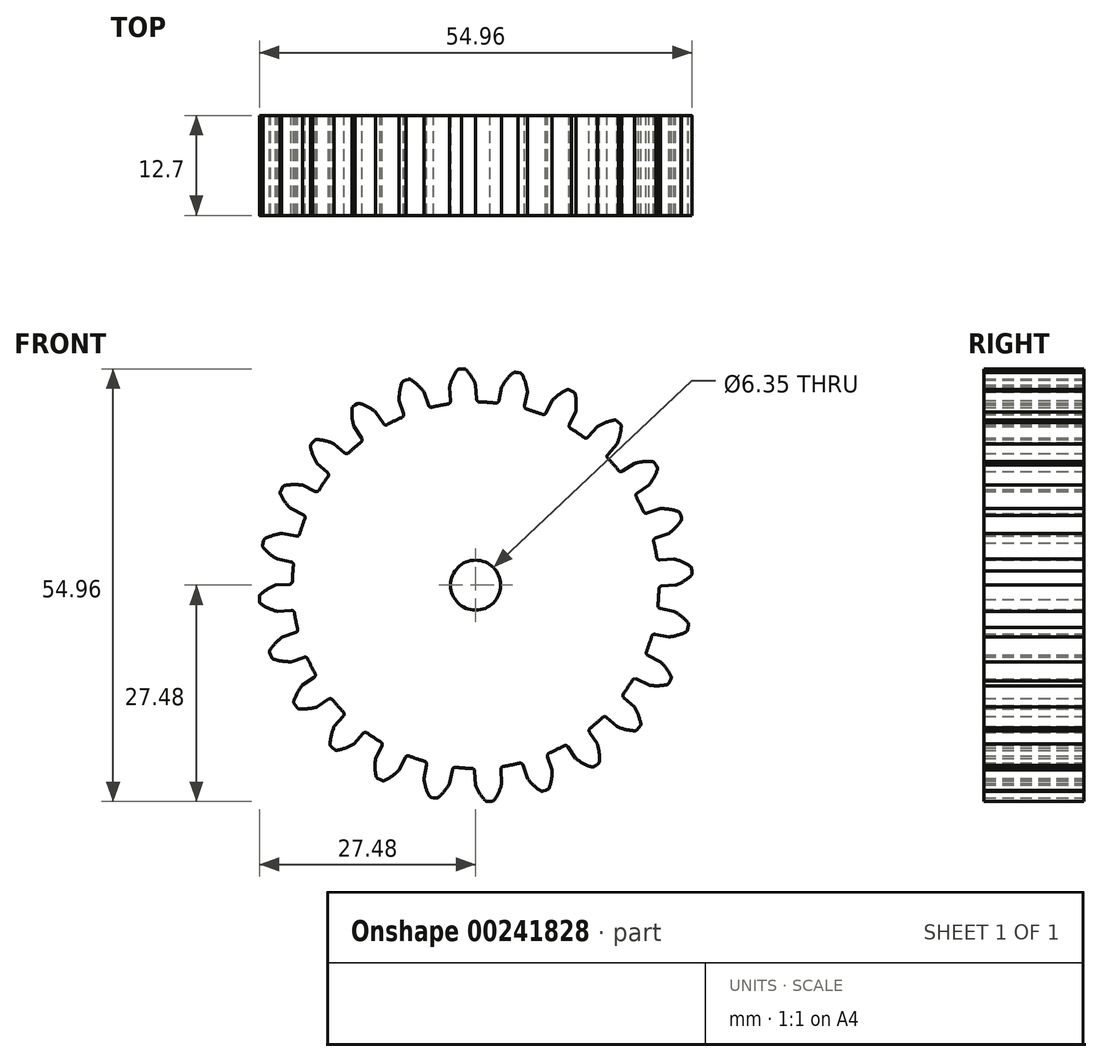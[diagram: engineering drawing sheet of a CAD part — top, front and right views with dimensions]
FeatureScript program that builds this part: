
annotation { "Feature Type Name" : "Feature", "Feature Type Description" : "" }
export const myFeature = defineFeature(function(context is Context, id is Id, definition is map)
    precondition{}
    {
        {
            var Q0;
            Q0=qCreatedBy(makeId("Front.planeOp"),FACE);
            var sketch = newSketch(context, id + "F0", { "sketchPlane" : qUnion([Q0])});
            skArc(sketch, "E0", {"start": v(-3.52, 23.02) * mm, "mid": v(-4.54, 22.84) * mm, "end": v(-5.55, 22.61) * mm});
            skArc(sketch, "E1.trimOffspring", {"start": v(0, 25.4) * mm, "mid": v(-0.5, 26.43) * mm, "end": v(-1.2, 27.35) * mm});
            skLineSegment(sketch, "E2", {"start": v(0, 25.4) * mm, "end": v(0.12, 23.63) * mm});
            skLineSegment(sketch, "E3", {"start": v(-1.5, 27.48) * mm, "end": v(-1.8, 27.46) * mm});
            skLineSegment(sketch, "E4.MirrorCS", {"start": v(-2.1, 27.44) * mm, "end": v(-1.8, 27.46) * mm});
            skArc(sketch, "E5.MirrorCS", {"start": v(-3.32, 25.18) * mm, "mid": v(-2.95, 26.27) * mm, "end": v(-2.39, 27.27) * mm});
            skLineSegment(sketch, "E6.MirrorCS", {"start": v(-3.32, 25.18) * mm, "end": v(-3.2, 23.42) * mm});
            skPoint(sketch, "E7.visualSharp", {"position": v(-2.28, 27.42) * mm});
            skArc(sketch, "E7.filletArc", {"start": v(-2.1, 27.44) * mm, "mid": v(-2.27, 27.39) * mm, "end": v(-2.39, 27.27) * mm});
            skPoint(sketch, "E8.visualSharp", {"position": v(-1.31, 27.49) * mm});
            skArc(sketch, "E8.filletArc", {"start": v(-1.2, 27.35) * mm, "mid": v(-1.33, 27.45) * mm, "end": v(-1.5, 27.48) * mm});
            skPoint(sketch, "E9.visualSharp", {"position": v(0.14, 23.28) * mm});
            skArc(sketch, "E9.filletArc", {"start": v(0.12, 23.63) * mm, "mid": v(0.23, 23.38) * mm, "end": v(0.49, 23.28) * mm});
            skPoint(sketch, "E10.visualSharp", {"position": v(-3.18, 23.07) * mm});
            skArc(sketch, "E10.filletArc", {"start": v(-3.52, 23.02) * mm, "mid": v(-3.28, 23.15) * mm, "end": v(-3.2, 23.42) * mm});
            skPoint(sketch, "E11.1.0", {"position": v(-8.38, 26.2) * mm});
            skPoint(sketch, "E11.1.1", {"position": v(-9.04, 21.46) * mm});
            skArc(sketch, "E11.1.2", {"start": v(-6.57, 24.53) * mm, "mid": v(-7.33, 25.4) * mm, "end": v(-8.23, 26.1) * mm});
            skArc(sketch, "E11.1.3", {"start": v(-9.72, 23.47) * mm, "mid": v(-9.65, 24.61) * mm, "end": v(-9.37, 25.72) * mm});
            skLineSegment(sketch, "E11.1.4", {"start": v(-9.72, 23.47) * mm, "end": v(-9.15, 21.8) * mm});
            skPoint(sketch, "E11.1.5", {"position": v(-9.3, 25.9) * mm});
            skLineSegment(sketch, "E11.1.6", {"start": v(-6.57, 24.53) * mm, "end": v(-6, 22.86) * mm});
            skLineSegment(sketch, "E11.1.7", {"start": v(-9.14, 25.96) * mm, "end": v(-8.85, 26.06) * mm});
            skArc(sketch, "E11.1.8", {"start": v(-9.14, 25.96) * mm, "mid": v(-9.28, 25.87) * mm, "end": v(-9.37, 25.72) * mm});
            skArc(sketch, "E11.1.9", {"start": v(-8.23, 26.1) * mm, "mid": v(-8.39, 26.17) * mm, "end": v(-8.55, 26.15) * mm});
            skLineSegment(sketch, "E11.1.10", {"start": v(-8.55, 26.15) * mm, "end": v(-8.85, 26.06) * mm});
            skArc(sketch, "E11.1.11", {"start": v(-6, 22.86) * mm, "mid": v(-5.83, 22.65) * mm, "end": v(-5.55, 22.61) * mm});
            skArc(sketch, "E11.1.12", {"start": v(-9.36, 21.32) * mm, "mid": v(-9.16, 21.51) * mm, "end": v(-9.15, 21.8) * mm});
            skPoint(sketch, "E11.2.0", {"position": v(-14.88, 23.15) * mm});
            skPoint(sketch, "E11.2.1", {"position": v(-14.28, 18.39) * mm});
            skArc(sketch, "E11.2.2", {"start": v(-12.7, 22) * mm, "mid": v(-13.65, 22.63) * mm, "end": v(-14.7, 23.1) * mm});
            skArc(sketch, "E11.2.3", {"start": v(-15.46, 20.15) * mm, "mid": v(-15.69, 21.28) * mm, "end": v(-15.7, 22.42) * mm});
            skLineSegment(sketch, "E11.2.4", {"start": v(-15.46, 20.15) * mm, "end": v(-14.48, 18.68) * mm});
            skPoint(sketch, "E11.2.5", {"position": v(-15.69, 22.6) * mm});
            skLineSegment(sketch, "E11.2.6", {"start": v(-12.7, 22) * mm, "end": v(-11.72, 20.53) * mm});
            skLineSegment(sketch, "E11.2.7", {"start": v(-15.54, 22.7) * mm, "end": v(-15.29, 22.88) * mm});
            skArc(sketch, "E11.2.8", {"start": v(-15.54, 22.7) * mm, "mid": v(-15.66, 22.58) * mm, "end": v(-15.7, 22.42) * mm});
            skArc(sketch, "E11.2.9", {"start": v(-14.7, 23.1) * mm, "mid": v(-14.87, 23.1) * mm, "end": v(-15.03, 23.05) * mm});
            skLineSegment(sketch, "E11.2.10", {"start": v(-15.03, 23.05) * mm, "end": v(-15.29, 22.88) * mm});
            skArc(sketch, "E11.2.11", {"start": v(-11.72, 20.53) * mm, "mid": v(-11.5, 20.37) * mm, "end": v(-11.22, 20.4) * mm});
            skArc(sketch, "E11.2.12", {"start": v(-14.56, 18.17) * mm, "mid": v(-14.42, 18.41) * mm, "end": v(-14.48, 18.68) * mm});
            skPoint(sketch, "E11.3.0", {"position": v(-20.36, 18.5) * mm});
            skPoint(sketch, "E11.3.1", {"position": v(-18.56, 14.06) * mm});
            skArc(sketch, "E11.3.2", {"start": v(-17.96, 17.96) * mm, "mid": v(-19.05, 18.33) * mm, "end": v(-20.18, 18.5) * mm});
            skArc(sketch, "E11.3.3", {"start": v(-20.15, 15.46) * mm, "mid": v(-20.66, 16.5) * mm, "end": v(-20.97, 17.6) * mm});
            skLineSegment(sketch, "E11.3.4", {"start": v(-20.15, 15.46) * mm, "end": v(-18.82, 14.3) * mm});
            skPoint(sketch, "E11.3.5", {"position": v(-21, 17.77) * mm});
            skLineSegment(sketch, "E11.3.6", {"start": v(-17.96, 17.96) * mm, "end": v(-16.63, 16.8) * mm});
            skLineSegment(sketch, "E11.3.7", {"start": v(-20.9, 17.91) * mm, "end": v(-20.7, 18.15) * mm});
            skArc(sketch, "E11.3.8", {"start": v(-20.9, 17.91) * mm, "mid": v(-20.97, 17.76) * mm, "end": v(-20.97, 17.6) * mm});
            skArc(sketch, "E11.3.9", {"start": v(-20.18, 18.5) * mm, "mid": v(-20.35, 18.47) * mm, "end": v(-20.48, 18.37) * mm});
            skLineSegment(sketch, "E11.3.10", {"start": v(-20.48, 18.37) * mm, "end": v(-20.7, 18.15) * mm});
            skArc(sketch, "E11.3.11", {"start": v(-16.63, 16.8) * mm, "mid": v(-16.37, 16.7) * mm, "end": v(-16.12, 16.8) * mm});
            skArc(sketch, "E11.3.12", {"start": v(-18.76, 13.78) * mm, "mid": v(-18.7, 14.05) * mm, "end": v(-18.82, 14.3) * mm});
            skPoint(sketch, "E11.4.0", {"position": v(-24.46, 12.6) * mm});
            skPoint(sketch, "E11.4.1", {"position": v(-21.56, 8.78) * mm});
            skArc(sketch, "E11.4.2", {"start": v(-22, 12.7) * mm, "mid": v(-23.14, 12.78) * mm, "end": v(-24.28, 12.64) * mm});
            skArc(sketch, "E11.4.3", {"start": v(-23.47, 9.72) * mm, "mid": v(-24.22, 10.58) * mm, "end": v(-24.81, 11.57) * mm});
            skLineSegment(sketch, "E11.4.4", {"start": v(-23.47, 9.72) * mm, "end": v(-21.88, 8.94) * mm});
            skPoint(sketch, "E11.4.5", {"position": v(-24.89, 11.73) * mm});
            skLineSegment(sketch, "E11.4.6", {"start": v(-22, 12.7) * mm, "end": v(-20.4, 11.92) * mm});
            skLineSegment(sketch, "E11.4.7", {"start": v(-24.81, 11.9) * mm, "end": v(-24.68, 12.17) * mm});
            skArc(sketch, "E11.4.8", {"start": v(-24.81, 11.9) * mm, "mid": v(-24.85, 11.73) * mm, "end": v(-24.81, 11.57) * mm});
            skArc(sketch, "E11.4.9", {"start": v(-24.28, 12.64) * mm, "mid": v(-24.43, 12.57) * mm, "end": v(-24.54, 12.45) * mm});
            skLineSegment(sketch, "E11.4.10", {"start": v(-24.54, 12.45) * mm, "end": v(-24.68, 12.17) * mm});
            skArc(sketch, "E11.4.11", {"start": v(-20.4, 11.92) * mm, "mid": v(-20.13, 11.9) * mm, "end": v(-19.92, 12.06) * mm});
            skArc(sketch, "E11.4.12", {"start": v(-21.7, 8.46) * mm, "mid": v(-21.7, 8.73) * mm, "end": v(-21.88, 8.94) * mm});
            skPoint(sketch, "E11.5.0", {"position": v(-26.89, 5.84) * mm});
            skPoint(sketch, "E11.5.1", {"position": v(-23.1, 2.9) * mm});
            skArc(sketch, "E11.5.2", {"start": v(-24.53, 6.57) * mm, "mid": v(-25.66, 6.35) * mm, "end": v(-26.73, 5.93) * mm});
            skArc(sketch, "E11.5.3", {"start": v(-25.18, 3.32) * mm, "mid": v(-26.14, 3.95) * mm, "end": v(-26.96, 4.75) * mm});
            skLineSegment(sketch, "E11.5.4", {"start": v(-25.18, 3.32) * mm, "end": v(-23.45, 2.97) * mm});
            skPoint(sketch, "E11.5.5", {"position": v(-27.08, 4.9) * mm});
            skLineSegment(sketch, "E11.5.6", {"start": v(-24.53, 6.57) * mm, "end": v(-22.8, 6.23) * mm});
            skLineSegment(sketch, "E11.5.7", {"start": v(-27.05, 5.07) * mm, "end": v(-27, 5.37) * mm});
            skArc(sketch, "E11.5.8", {"start": v(-27.05, 5.07) * mm, "mid": v(-27.04, 4.9) * mm, "end": v(-26.96, 4.75) * mm});
            skArc(sketch, "E11.5.9", {"start": v(-26.73, 5.93) * mm, "mid": v(-26.86, 5.82) * mm, "end": v(-26.93, 5.67) * mm});
            skLineSegment(sketch, "E11.5.10", {"start": v(-26.93, 5.67) * mm, "end": v(-27, 5.37) * mm});
            skArc(sketch, "E11.5.11", {"start": v(-22.8, 6.23) * mm, "mid": v(-22.53, 6.28) * mm, "end": v(-22.36, 6.5) * mm});
            skArc(sketch, "E11.5.12", {"start": v(-23.14, 2.55) * mm, "mid": v(-23.21, 2.82) * mm, "end": v(-23.45, 2.97) * mm});
            skPoint(sketch, "E11.6.0", {"position": v(-27.49, -1.31) * mm});
            skPoint(sketch, "E11.6.1", {"position": v(-23.07, -3.18) * mm});
            skArc(sketch, "E11.6.2", {"start": v(-25.4, 0) * mm, "mid": v(-26.43, -0.5) * mm, "end": v(-27.35, -1.2) * mm});
            skArc(sketch, "E11.6.3", {"start": v(-25.18, -3.32) * mm, "mid": v(-26.27, -2.95) * mm, "end": v(-27.27, -2.39) * mm});
            skLineSegment(sketch, "E11.6.4", {"start": v(-25.18, -3.32) * mm, "end": v(-23.42, -3.2) * mm});
            skPoint(sketch, "E11.6.5", {"position": v(-27.42, -2.28) * mm});
            skLineSegment(sketch, "E11.6.6", {"start": v(-25.4, 0) * mm, "end": v(-23.63, 0.12) * mm});
            skLineSegment(sketch, "E11.6.7", {"start": v(-27.44, -2.1) * mm, "end": v(-27.46, -1.8) * mm});
            skArc(sketch, "E11.6.8", {"start": v(-27.44, -2.1) * mm, "mid": v(-27.39, -2.27) * mm, "end": v(-27.27, -2.39) * mm});
            skArc(sketch, "E11.6.9", {"start": v(-27.35, -1.2) * mm, "mid": v(-27.45, -1.33) * mm, "end": v(-27.48, -1.5) * mm});
            skLineSegment(sketch, "E11.6.10", {"start": v(-27.48, -1.5) * mm, "end": v(-27.46, -1.8) * mm});
            skArc(sketch, "E11.6.11", {"start": v(-23.63, 0.12) * mm, "mid": v(-23.38, 0.23) * mm, "end": v(-23.28, 0.49) * mm});
            skArc(sketch, "E11.6.12", {"start": v(-23.02, -3.52) * mm, "mid": v(-23.15, -3.28) * mm, "end": v(-23.42, -3.2) * mm});
            skPoint(sketch, "E11.7.0", {"position": v(-26.2, -8.38) * mm});
            skPoint(sketch, "E11.7.1", {"position": v(-21.46, -9.04) * mm});
            skArc(sketch, "E11.7.2", {"start": v(-24.53, -6.57) * mm, "mid": v(-25.4, -7.33) * mm, "end": v(-26.1, -8.23) * mm});
            skArc(sketch, "E11.7.3", {"start": v(-23.47, -9.72) * mm, "mid": v(-24.61, -9.65) * mm, "end": v(-25.72, -9.37) * mm});
            skLineSegment(sketch, "E11.7.4", {"start": v(-23.47, -9.72) * mm, "end": v(-21.8, -9.15) * mm});
            skPoint(sketch, "E11.7.5", {"position": v(-25.9, -9.3) * mm});
            skLineSegment(sketch, "E11.7.6", {"start": v(-24.53, -6.57) * mm, "end": v(-22.86, -6) * mm});
            skLineSegment(sketch, "E11.7.7", {"start": v(-25.96, -9.14) * mm, "end": v(-26.06, -8.85) * mm});
            skArc(sketch, "E11.7.8", {"start": v(-25.96, -9.14) * mm, "mid": v(-25.87, -9.28) * mm, "end": v(-25.72, -9.37) * mm});
            skArc(sketch, "E11.7.9", {"start": v(-26.1, -8.23) * mm, "mid": v(-26.17, -8.39) * mm, "end": v(-26.15, -8.55) * mm});
            skLineSegment(sketch, "E11.7.10", {"start": v(-26.15, -8.55) * mm, "end": v(-26.06, -8.85) * mm});
            skArc(sketch, "E11.7.11", {"start": v(-22.86, -6) * mm, "mid": v(-22.65, -5.83) * mm, "end": v(-22.61, -5.55) * mm});
            skArc(sketch, "E11.7.12", {"start": v(-21.32, -9.36) * mm, "mid": v(-21.51, -9.16) * mm, "end": v(-21.8, -9.15) * mm});
            skPoint(sketch, "E11.8.0", {"position": v(-23.15, -14.88) * mm});
            skPoint(sketch, "E11.8.1", {"position": v(-18.39, -14.28) * mm});
            skArc(sketch, "E11.8.2", {"start": v(-22, -12.7) * mm, "mid": v(-22.63, -13.65) * mm, "end": v(-23.1, -14.7) * mm});
            skArc(sketch, "E11.8.3", {"start": v(-20.15, -15.46) * mm, "mid": v(-21.28, -15.69) * mm, "end": v(-22.42, -15.7) * mm});
            skLineSegment(sketch, "E11.8.4", {"start": v(-20.15, -15.46) * mm, "end": v(-18.68, -14.48) * mm});
            skPoint(sketch, "E11.8.5", {"position": v(-22.6, -15.69) * mm});
            skLineSegment(sketch, "E11.8.6", {"start": v(-22, -12.7) * mm, "end": v(-20.53, -11.72) * mm});
            skLineSegment(sketch, "E11.8.7", {"start": v(-22.7, -15.54) * mm, "end": v(-22.88, -15.29) * mm});
            skArc(sketch, "E11.8.8", {"start": v(-22.7, -15.54) * mm, "mid": v(-22.58, -15.66) * mm, "end": v(-22.42, -15.7) * mm});
            skArc(sketch, "E11.8.9", {"start": v(-23.1, -14.7) * mm, "mid": v(-23.1, -14.87) * mm, "end": v(-23.05, -15.03) * mm});
            skLineSegment(sketch, "E11.8.10", {"start": v(-23.05, -15.03) * mm, "end": v(-22.88, -15.29) * mm});
            skArc(sketch, "E11.8.11", {"start": v(-20.53, -11.72) * mm, "mid": v(-20.37, -11.5) * mm, "end": v(-20.4, -11.22) * mm});
            skArc(sketch, "E11.8.12", {"start": v(-18.17, -14.56) * mm, "mid": v(-18.41, -14.42) * mm, "end": v(-18.68, -14.48) * mm});
            skPoint(sketch, "E11.9.0", {"position": v(-18.5, -20.36) * mm});
            skPoint(sketch, "E11.9.1", {"position": v(-14.06, -18.56) * mm});
            skArc(sketch, "E11.9.2", {"start": v(-17.96, -17.96) * mm, "mid": v(-18.33, -19.05) * mm, "end": v(-18.5, -20.18) * mm});
            skArc(sketch, "E11.9.3", {"start": v(-15.46, -20.15) * mm, "mid": v(-16.5, -20.66) * mm, "end": v(-17.6, -20.97) * mm});
            skLineSegment(sketch, "E11.9.4", {"start": v(-15.46, -20.15) * mm, "end": v(-14.3, -18.82) * mm});
            skPoint(sketch, "E11.9.5", {"position": v(-17.77, -21) * mm});
            skLineSegment(sketch, "E11.9.6", {"start": v(-17.96, -17.96) * mm, "end": v(-16.8, -16.63) * mm});
            skLineSegment(sketch, "E11.9.7", {"start": v(-17.91, -20.9) * mm, "end": v(-18.15, -20.7) * mm});
            skArc(sketch, "E11.9.8", {"start": v(-17.91, -20.9) * mm, "mid": v(-17.76, -20.97) * mm, "end": v(-17.6, -20.97) * mm});
            skArc(sketch, "E11.9.9", {"start": v(-18.5, -20.18) * mm, "mid": v(-18.47, -20.35) * mm, "end": v(-18.37, -20.48) * mm});
            skLineSegment(sketch, "E11.9.10", {"start": v(-18.37, -20.48) * mm, "end": v(-18.15, -20.7) * mm});
            skArc(sketch, "E11.9.11", {"start": v(-16.8, -16.63) * mm, "mid": v(-16.7, -16.37) * mm, "end": v(-16.8, -16.12) * mm});
            skArc(sketch, "E11.9.12", {"start": v(-13.78, -18.76) * mm, "mid": v(-14.05, -18.7) * mm, "end": v(-14.3, -18.82) * mm});
            skPoint(sketch, "E11.10.0", {"position": v(-12.6, -24.46) * mm});
            skPoint(sketch, "E11.10.1", {"position": v(-8.78, -21.56) * mm});
            skArc(sketch, "E11.10.2", {"start": v(-12.7, -22) * mm, "mid": v(-12.78, -23.14) * mm, "end": v(-12.64, -24.28) * mm});
            skArc(sketch, "E11.10.3", {"start": v(-9.72, -23.47) * mm, "mid": v(-10.58, -24.22) * mm, "end": v(-11.57, -24.81) * mm});
            skLineSegment(sketch, "E11.10.4", {"start": v(-9.72, -23.47) * mm, "end": v(-8.94, -21.88) * mm});
            skPoint(sketch, "E11.10.5", {"position": v(-11.73, -24.89) * mm});
            skLineSegment(sketch, "E11.10.6", {"start": v(-12.7, -22) * mm, "end": v(-11.92, -20.4) * mm});
            skLineSegment(sketch, "E11.10.7", {"start": v(-11.9, -24.81) * mm, "end": v(-12.17, -24.68) * mm});
            skArc(sketch, "E11.10.8", {"start": v(-11.9, -24.81) * mm, "mid": v(-11.73, -24.85) * mm, "end": v(-11.57, -24.81) * mm});
            skArc(sketch, "E11.10.9", {"start": v(-12.64, -24.28) * mm, "mid": v(-12.57, -24.43) * mm, "end": v(-12.45, -24.54) * mm});
            skLineSegment(sketch, "E11.10.10", {"start": v(-12.45, -24.54) * mm, "end": v(-12.17, -24.68) * mm});
            skArc(sketch, "E11.10.11", {"start": v(-11.92, -20.4) * mm, "mid": v(-11.9, -20.13) * mm, "end": v(-12.06, -19.92) * mm});
            skArc(sketch, "E11.10.12", {"start": v(-8.46, -21.7) * mm, "mid": v(-8.73, -21.7) * mm, "end": v(-8.94, -21.88) * mm});
            skPoint(sketch, "E11.11.0", {"position": v(-5.84, -26.89) * mm});
            skPoint(sketch, "E11.11.1", {"position": v(-2.9, -23.1) * mm});
            skArc(sketch, "E11.11.2", {"start": v(-6.57, -24.53) * mm, "mid": v(-6.35, -25.66) * mm, "end": v(-5.93, -26.73) * mm});
            skArc(sketch, "E11.11.3", {"start": v(-3.32, -25.18) * mm, "mid": v(-3.95, -26.14) * mm, "end": v(-4.75, -26.96) * mm});
            skLineSegment(sketch, "E11.11.4", {"start": v(-3.32, -25.18) * mm, "end": v(-2.97, -23.45) * mm});
            skPoint(sketch, "E11.11.5", {"position": v(-4.9, -27.08) * mm});
            skLineSegment(sketch, "E11.11.6", {"start": v(-6.57, -24.53) * mm, "end": v(-6.23, -22.8) * mm});
            skLineSegment(sketch, "E11.11.7", {"start": v(-5.07, -27.05) * mm, "end": v(-5.37, -27) * mm});
            skArc(sketch, "E11.11.8", {"start": v(-5.07, -27.05) * mm, "mid": v(-4.9, -27.04) * mm, "end": v(-4.75, -26.96) * mm});
            skArc(sketch, "E11.11.9", {"start": v(-5.93, -26.73) * mm, "mid": v(-5.82, -26.86) * mm, "end": v(-5.67, -26.93) * mm});
            skLineSegment(sketch, "E11.11.10", {"start": v(-5.67, -26.93) * mm, "end": v(-5.37, -27) * mm});
            skArc(sketch, "E11.11.11", {"start": v(-6.23, -22.8) * mm, "mid": v(-6.28, -22.53) * mm, "end": v(-6.5, -22.36) * mm});
            skArc(sketch, "E11.11.12", {"start": v(-2.55, -23.14) * mm, "mid": v(-2.82, -23.21) * mm, "end": v(-2.97, -23.45) * mm});
            skPoint(sketch, "E11.12.0", {"position": v(1.31, -27.49) * mm});
            skPoint(sketch, "E11.12.1", {"position": v(3.18, -23.07) * mm});
            skArc(sketch, "E11.12.2", {"start": v(0, -25.4) * mm, "mid": v(0.5, -26.43) * mm, "end": v(1.2, -27.35) * mm});
            skArc(sketch, "E11.12.3", {"start": v(3.32, -25.18) * mm, "mid": v(2.95, -26.27) * mm, "end": v(2.39, -27.27) * mm});
            skLineSegment(sketch, "E11.12.4", {"start": v(3.32, -25.18) * mm, "end": v(3.2, -23.42) * mm});
            skPoint(sketch, "E11.12.5", {"position": v(2.28, -27.42) * mm});
            skLineSegment(sketch, "E11.12.6", {"start": v(0, -25.4) * mm, "end": v(-0.12, -23.63) * mm});
            skLineSegment(sketch, "E11.12.7", {"start": v(2.1, -27.44) * mm, "end": v(1.8, -27.46) * mm});
            skArc(sketch, "E11.12.8", {"start": v(2.1, -27.44) * mm, "mid": v(2.27, -27.39) * mm, "end": v(2.39, -27.27) * mm});
            skArc(sketch, "E11.12.9", {"start": v(1.2, -27.35) * mm, "mid": v(1.33, -27.45) * mm, "end": v(1.5, -27.48) * mm});
            skLineSegment(sketch, "E11.12.10", {"start": v(1.5, -27.48) * mm, "end": v(1.8, -27.46) * mm});
            skArc(sketch, "E11.12.11", {"start": v(-0.12, -23.63) * mm, "mid": v(-0.23, -23.38) * mm, "end": v(-0.49, -23.28) * mm});
            skArc(sketch, "E11.12.12", {"start": v(3.52, -23.02) * mm, "mid": v(3.28, -23.15) * mm, "end": v(3.2, -23.42) * mm});
            skPoint(sketch, "E11.13.0", {"position": v(8.38, -26.2) * mm});
            skPoint(sketch, "E11.13.1", {"position": v(9.04, -21.46) * mm});
            skArc(sketch, "E11.13.2", {"start": v(6.57, -24.53) * mm, "mid": v(7.33, -25.4) * mm, "end": v(8.23, -26.1) * mm});
            skArc(sketch, "E11.13.3", {"start": v(9.72, -23.47) * mm, "mid": v(9.65, -24.61) * mm, "end": v(9.37, -25.72) * mm});
            skLineSegment(sketch, "E11.13.4", {"start": v(9.72, -23.47) * mm, "end": v(9.15, -21.8) * mm});
            skPoint(sketch, "E11.13.5", {"position": v(9.3, -25.9) * mm});
            skLineSegment(sketch, "E11.13.6", {"start": v(6.57, -24.53) * mm, "end": v(6, -22.86) * mm});
            skLineSegment(sketch, "E11.13.7", {"start": v(9.14, -25.96) * mm, "end": v(8.85, -26.06) * mm});
            skArc(sketch, "E11.13.8", {"start": v(9.14, -25.96) * mm, "mid": v(9.28, -25.87) * mm, "end": v(9.37, -25.72) * mm});
            skArc(sketch, "E11.13.9", {"start": v(8.23, -26.1) * mm, "mid": v(8.39, -26.17) * mm, "end": v(8.55, -26.15) * mm});
            skLineSegment(sketch, "E11.13.10", {"start": v(8.55, -26.15) * mm, "end": v(8.85, -26.06) * mm});
            skArc(sketch, "E11.13.11", {"start": v(6, -22.86) * mm, "mid": v(5.83, -22.65) * mm, "end": v(5.55, -22.61) * mm});
            skArc(sketch, "E11.13.12", {"start": v(9.36, -21.32) * mm, "mid": v(9.16, -21.51) * mm, "end": v(9.15, -21.8) * mm});
            skPoint(sketch, "E11.14.0", {"position": v(14.88, -23.15) * mm});
            skPoint(sketch, "E11.14.1", {"position": v(14.28, -18.39) * mm});
            skArc(sketch, "E11.14.2", {"start": v(12.7, -22) * mm, "mid": v(13.65, -22.63) * mm, "end": v(14.7, -23.1) * mm});
            skArc(sketch, "E11.14.3", {"start": v(15.46, -20.15) * mm, "mid": v(15.69, -21.28) * mm, "end": v(15.7, -22.42) * mm});
            skLineSegment(sketch, "E11.14.4", {"start": v(15.46, -20.15) * mm, "end": v(14.48, -18.68) * mm});
            skPoint(sketch, "E11.14.5", {"position": v(15.69, -22.6) * mm});
            skLineSegment(sketch, "E11.14.6", {"start": v(12.7, -22) * mm, "end": v(11.72, -20.53) * mm});
            skLineSegment(sketch, "E11.14.7", {"start": v(15.54, -22.7) * mm, "end": v(15.29, -22.88) * mm});
            skArc(sketch, "E11.14.8", {"start": v(15.54, -22.7) * mm, "mid": v(15.66, -22.58) * mm, "end": v(15.7, -22.42) * mm});
            skArc(sketch, "E11.14.9", {"start": v(14.7, -23.1) * mm, "mid": v(14.87, -23.1) * mm, "end": v(15.03, -23.05) * mm});
            skLineSegment(sketch, "E11.14.10", {"start": v(15.03, -23.05) * mm, "end": v(15.29, -22.88) * mm});
            skArc(sketch, "E11.14.11", {"start": v(11.72, -20.53) * mm, "mid": v(11.5, -20.37) * mm, "end": v(11.22, -20.4) * mm});
            skArc(sketch, "E11.14.12", {"start": v(14.56, -18.17) * mm, "mid": v(14.42, -18.41) * mm, "end": v(14.48, -18.68) * mm});
            skPoint(sketch, "E11.15.0", {"position": v(20.36, -18.5) * mm});
            skPoint(sketch, "E11.15.1", {"position": v(18.56, -14.06) * mm});
            skArc(sketch, "E11.15.2", {"start": v(17.96, -17.96) * mm, "mid": v(19.05, -18.33) * mm, "end": v(20.18, -18.5) * mm});
            skArc(sketch, "E11.15.3", {"start": v(20.15, -15.46) * mm, "mid": v(20.66, -16.5) * mm, "end": v(20.97, -17.6) * mm});
            skLineSegment(sketch, "E11.15.4", {"start": v(20.15, -15.46) * mm, "end": v(18.82, -14.3) * mm});
            skPoint(sketch, "E11.15.5", {"position": v(21, -17.77) * mm});
            skLineSegment(sketch, "E11.15.6", {"start": v(17.96, -17.96) * mm, "end": v(16.63, -16.8) * mm});
            skLineSegment(sketch, "E11.15.7", {"start": v(20.9, -17.91) * mm, "end": v(20.7, -18.15) * mm});
            skArc(sketch, "E11.15.8", {"start": v(20.9, -17.91) * mm, "mid": v(20.97, -17.76) * mm, "end": v(20.97, -17.6) * mm});
            skArc(sketch, "E11.15.9", {"start": v(20.18, -18.5) * mm, "mid": v(20.35, -18.47) * mm, "end": v(20.48, -18.37) * mm});
            skLineSegment(sketch, "E11.15.10", {"start": v(20.48, -18.37) * mm, "end": v(20.7, -18.15) * mm});
            skArc(sketch, "E11.15.11", {"start": v(16.63, -16.8) * mm, "mid": v(16.37, -16.7) * mm, "end": v(16.12, -16.8) * mm});
            skArc(sketch, "E11.15.12", {"start": v(18.76, -13.78) * mm, "mid": v(18.7, -14.05) * mm, "end": v(18.82, -14.3) * mm});
            skPoint(sketch, "E11.16.0", {"position": v(24.46, -12.6) * mm});
            skPoint(sketch, "E11.16.1", {"position": v(21.56, -8.78) * mm});
            skArc(sketch, "E11.16.2", {"start": v(22, -12.7) * mm, "mid": v(23.14, -12.78) * mm, "end": v(24.28, -12.64) * mm});
            skArc(sketch, "E11.16.3", {"start": v(23.47, -9.72) * mm, "mid": v(24.22, -10.58) * mm, "end": v(24.81, -11.57) * mm});
            skLineSegment(sketch, "E11.16.4", {"start": v(23.47, -9.72) * mm, "end": v(21.88, -8.94) * mm});
            skPoint(sketch, "E11.16.5", {"position": v(24.89, -11.73) * mm});
            skLineSegment(sketch, "E11.16.6", {"start": v(22, -12.7) * mm, "end": v(20.4, -11.92) * mm});
            skLineSegment(sketch, "E11.16.7", {"start": v(24.81, -11.9) * mm, "end": v(24.68, -12.17) * mm});
            skArc(sketch, "E11.16.8", {"start": v(24.81, -11.9) * mm, "mid": v(24.85, -11.73) * mm, "end": v(24.81, -11.57) * mm});
            skArc(sketch, "E11.16.9", {"start": v(24.28, -12.64) * mm, "mid": v(24.43, -12.57) * mm, "end": v(24.54, -12.45) * mm});
            skLineSegment(sketch, "E11.16.10", {"start": v(24.54, -12.45) * mm, "end": v(24.68, -12.17) * mm});
            skArc(sketch, "E11.16.11", {"start": v(20.4, -11.92) * mm, "mid": v(20.13, -11.9) * mm, "end": v(19.92, -12.06) * mm});
            skArc(sketch, "E11.16.12", {"start": v(21.7, -8.46) * mm, "mid": v(21.7, -8.73) * mm, "end": v(21.88, -8.94) * mm});
            skPoint(sketch, "E11.17.0", {"position": v(26.89, -5.84) * mm});
            skPoint(sketch, "E11.17.1", {"position": v(23.1, -2.9) * mm});
            skArc(sketch, "E11.17.2", {"start": v(24.53, -6.57) * mm, "mid": v(25.66, -6.35) * mm, "end": v(26.73, -5.93) * mm});
            skArc(sketch, "E11.17.3", {"start": v(25.18, -3.32) * mm, "mid": v(26.14, -3.95) * mm, "end": v(26.96, -4.75) * mm});
            skLineSegment(sketch, "E11.17.4", {"start": v(25.18, -3.32) * mm, "end": v(23.45, -2.97) * mm});
            skPoint(sketch, "E11.17.5", {"position": v(27.08, -4.9) * mm});
            skLineSegment(sketch, "E11.17.6", {"start": v(24.53, -6.57) * mm, "end": v(22.8, -6.23) * mm});
            skLineSegment(sketch, "E11.17.7", {"start": v(27.05, -5.07) * mm, "end": v(27, -5.37) * mm});
            skArc(sketch, "E11.17.8", {"start": v(27.05, -5.07) * mm, "mid": v(27.04, -4.9) * mm, "end": v(26.96, -4.75) * mm});
            skArc(sketch, "E11.17.9", {"start": v(26.73, -5.93) * mm, "mid": v(26.86, -5.82) * mm, "end": v(26.93, -5.67) * mm});
            skLineSegment(sketch, "E11.17.10", {"start": v(26.93, -5.67) * mm, "end": v(27, -5.37) * mm});
            skArc(sketch, "E11.17.11", {"start": v(22.8, -6.23) * mm, "mid": v(22.53, -6.28) * mm, "end": v(22.36, -6.5) * mm});
            skArc(sketch, "E11.17.12", {"start": v(23.14, -2.55) * mm, "mid": v(23.21, -2.82) * mm, "end": v(23.45, -2.97) * mm});
            skPoint(sketch, "E11.18.0", {"position": v(27.49, 1.31) * mm});
            skPoint(sketch, "E11.18.1", {"position": v(23.07, 3.18) * mm});
            skArc(sketch, "E11.18.2", {"start": v(25.4, 0) * mm, "mid": v(26.43, 0.5) * mm, "end": v(27.35, 1.2) * mm});
            skArc(sketch, "E11.18.3", {"start": v(25.18, 3.32) * mm, "mid": v(26.27, 2.95) * mm, "end": v(27.27, 2.39) * mm});
            skLineSegment(sketch, "E11.18.4", {"start": v(25.18, 3.32) * mm, "end": v(23.42, 3.2) * mm});
            skPoint(sketch, "E11.18.5", {"position": v(27.42, 2.28) * mm});
            skLineSegment(sketch, "E11.18.6", {"start": v(25.4, 0) * mm, "end": v(23.63, -0.12) * mm});
            skLineSegment(sketch, "E11.18.7", {"start": v(27.44, 2.1) * mm, "end": v(27.46, 1.8) * mm});
            skArc(sketch, "E11.18.8", {"start": v(27.44, 2.1) * mm, "mid": v(27.39, 2.27) * mm, "end": v(27.27, 2.39) * mm});
            skArc(sketch, "E11.18.9", {"start": v(27.35, 1.2) * mm, "mid": v(27.45, 1.33) * mm, "end": v(27.48, 1.5) * mm});
            skLineSegment(sketch, "E11.18.10", {"start": v(27.48, 1.5) * mm, "end": v(27.46, 1.8) * mm});
            skArc(sketch, "E11.18.11", {"start": v(23.63, -0.12) * mm, "mid": v(23.38, -0.23) * mm, "end": v(23.28, -0.49) * mm});
            skArc(sketch, "E11.18.12", {"start": v(23.02, 3.52) * mm, "mid": v(23.15, 3.28) * mm, "end": v(23.42, 3.2) * mm});
            skPoint(sketch, "E11.19.0", {"position": v(26.2, 8.38) * mm});
            skPoint(sketch, "E11.19.1", {"position": v(21.46, 9.04) * mm});
            skArc(sketch, "E11.19.2", {"start": v(24.53, 6.57) * mm, "mid": v(25.4, 7.33) * mm, "end": v(26.1, 8.23) * mm});
            skArc(sketch, "E11.19.3", {"start": v(23.47, 9.72) * mm, "mid": v(24.61, 9.65) * mm, "end": v(25.72, 9.37) * mm});
            skLineSegment(sketch, "E11.19.4", {"start": v(23.47, 9.72) * mm, "end": v(21.8, 9.15) * mm});
            skPoint(sketch, "E11.19.5", {"position": v(25.9, 9.3) * mm});
            skLineSegment(sketch, "E11.19.6", {"start": v(24.53, 6.57) * mm, "end": v(22.86, 6) * mm});
            skLineSegment(sketch, "E11.19.7", {"start": v(25.96, 9.14) * mm, "end": v(26.06, 8.85) * mm});
            skArc(sketch, "E11.19.8", {"start": v(25.96, 9.14) * mm, "mid": v(25.87, 9.28) * mm, "end": v(25.72, 9.37) * mm});
            skArc(sketch, "E11.19.9", {"start": v(26.1, 8.23) * mm, "mid": v(26.17, 8.39) * mm, "end": v(26.15, 8.55) * mm});
            skLineSegment(sketch, "E11.19.10", {"start": v(26.15, 8.55) * mm, "end": v(26.06, 8.85) * mm});
            skArc(sketch, "E11.19.11", {"start": v(22.86, 6) * mm, "mid": v(22.65, 5.83) * mm, "end": v(22.61, 5.55) * mm});
            skArc(sketch, "E11.19.12", {"start": v(21.32, 9.36) * mm, "mid": v(21.51, 9.16) * mm, "end": v(21.8, 9.15) * mm});
            skPoint(sketch, "E11.20.0", {"position": v(23.15, 14.88) * mm});
            skPoint(sketch, "E11.20.1", {"position": v(18.39, 14.28) * mm});
            skArc(sketch, "E11.20.2", {"start": v(22, 12.7) * mm, "mid": v(22.63, 13.65) * mm, "end": v(23.1, 14.7) * mm});
            skArc(sketch, "E11.20.3", {"start": v(20.15, 15.46) * mm, "mid": v(21.28, 15.69) * mm, "end": v(22.42, 15.7) * mm});
            skLineSegment(sketch, "E11.20.4", {"start": v(20.15, 15.46) * mm, "end": v(18.68, 14.48) * mm});
            skPoint(sketch, "E11.20.5", {"position": v(22.6, 15.69) * mm});
            skLineSegment(sketch, "E11.20.6", {"start": v(22, 12.7) * mm, "end": v(20.53, 11.72) * mm});
            skLineSegment(sketch, "E11.20.7", {"start": v(22.7, 15.54) * mm, "end": v(22.88, 15.29) * mm});
            skArc(sketch, "E11.20.8", {"start": v(22.7, 15.54) * mm, "mid": v(22.58, 15.66) * mm, "end": v(22.42, 15.7) * mm});
            skArc(sketch, "E11.20.9", {"start": v(23.1, 14.7) * mm, "mid": v(23.1, 14.87) * mm, "end": v(23.05, 15.03) * mm});
            skLineSegment(sketch, "E11.20.10", {"start": v(23.05, 15.03) * mm, "end": v(22.88, 15.29) * mm});
            skArc(sketch, "E11.20.11", {"start": v(20.53, 11.72) * mm, "mid": v(20.37, 11.5) * mm, "end": v(20.4, 11.22) * mm});
            skArc(sketch, "E11.20.12", {"start": v(18.17, 14.56) * mm, "mid": v(18.41, 14.42) * mm, "end": v(18.68, 14.48) * mm});
            skPoint(sketch, "E11.21.0", {"position": v(18.5, 20.36) * mm});
            skPoint(sketch, "E11.21.1", {"position": v(14.06, 18.56) * mm});
            skArc(sketch, "E11.21.2", {"start": v(17.96, 17.96) * mm, "mid": v(18.33, 19.05) * mm, "end": v(18.5, 20.18) * mm});
            skArc(sketch, "E11.21.3", {"start": v(15.46, 20.15) * mm, "mid": v(16.5, 20.66) * mm, "end": v(17.6, 20.97) * mm});
            skLineSegment(sketch, "E11.21.4", {"start": v(15.46, 20.15) * mm, "end": v(14.3, 18.82) * mm});
            skPoint(sketch, "E11.21.5", {"position": v(17.77, 21) * mm});
            skLineSegment(sketch, "E11.21.6", {"start": v(17.96, 17.96) * mm, "end": v(16.8, 16.63) * mm});
            skLineSegment(sketch, "E11.21.7", {"start": v(17.91, 20.9) * mm, "end": v(18.15, 20.7) * mm});
            skArc(sketch, "E11.21.8", {"start": v(17.91, 20.9) * mm, "mid": v(17.76, 20.97) * mm, "end": v(17.6, 20.97) * mm});
            skArc(sketch, "E11.21.9", {"start": v(18.5, 20.18) * mm, "mid": v(18.47, 20.35) * mm, "end": v(18.37, 20.48) * mm});
            skLineSegment(sketch, "E11.21.10", {"start": v(18.37, 20.48) * mm, "end": v(18.15, 20.7) * mm});
            skArc(sketch, "E11.21.11", {"start": v(16.8, 16.63) * mm, "mid": v(16.7, 16.37) * mm, "end": v(16.8, 16.12) * mm});
            skArc(sketch, "E11.21.12", {"start": v(13.78, 18.76) * mm, "mid": v(14.05, 18.7) * mm, "end": v(14.3, 18.82) * mm});
            skPoint(sketch, "E11.22.0", {"position": v(12.6, 24.46) * mm});
            skPoint(sketch, "E11.22.1", {"position": v(8.78, 21.56) * mm});
            skArc(sketch, "E11.22.2", {"start": v(12.7, 22) * mm, "mid": v(12.78, 23.14) * mm, "end": v(12.64, 24.28) * mm});
            skArc(sketch, "E11.22.3", {"start": v(9.72, 23.47) * mm, "mid": v(10.58, 24.22) * mm, "end": v(11.57, 24.81) * mm});
            skLineSegment(sketch, "E11.22.4", {"start": v(9.72, 23.47) * mm, "end": v(8.94, 21.88) * mm});
            skPoint(sketch, "E11.22.5", {"position": v(11.73, 24.89) * mm});
            skLineSegment(sketch, "E11.22.6", {"start": v(12.7, 22) * mm, "end": v(11.92, 20.4) * mm});
            skLineSegment(sketch, "E11.22.7", {"start": v(11.9, 24.81) * mm, "end": v(12.17, 24.68) * mm});
            skArc(sketch, "E11.22.8", {"start": v(11.9, 24.81) * mm, "mid": v(11.73, 24.85) * mm, "end": v(11.57, 24.81) * mm});
            skArc(sketch, "E11.22.9", {"start": v(12.64, 24.28) * mm, "mid": v(12.57, 24.43) * mm, "end": v(12.45, 24.54) * mm});
            skLineSegment(sketch, "E11.22.10", {"start": v(12.45, 24.54) * mm, "end": v(12.17, 24.68) * mm});
            skArc(sketch, "E11.22.11", {"start": v(11.92, 20.4) * mm, "mid": v(11.9, 20.13) * mm, "end": v(12.06, 19.92) * mm});
            skArc(sketch, "E11.22.12", {"start": v(8.46, 21.7) * mm, "mid": v(8.73, 21.7) * mm, "end": v(8.94, 21.88) * mm});
            skPoint(sketch, "E11.23.0", {"position": v(5.84, 26.89) * mm});
            skPoint(sketch, "E11.23.1", {"position": v(2.9, 23.1) * mm});
            skArc(sketch, "E11.23.2", {"start": v(6.57, 24.53) * mm, "mid": v(6.35, 25.66) * mm, "end": v(5.93, 26.73) * mm});
            skArc(sketch, "E11.23.3", {"start": v(3.32, 25.18) * mm, "mid": v(3.95, 26.14) * mm, "end": v(4.75, 26.96) * mm});
            skLineSegment(sketch, "E11.23.4", {"start": v(3.32, 25.18) * mm, "end": v(2.97, 23.45) * mm});
            skPoint(sketch, "E11.23.5", {"position": v(4.9, 27.08) * mm});
            skLineSegment(sketch, "E11.23.6", {"start": v(6.57, 24.53) * mm, "end": v(6.23, 22.8) * mm});
            skLineSegment(sketch, "E11.23.7", {"start": v(5.07, 27.05) * mm, "end": v(5.37, 27) * mm});
            skArc(sketch, "E11.23.8", {"start": v(5.07, 27.05) * mm, "mid": v(4.9, 27.04) * mm, "end": v(4.75, 26.96) * mm});
            skArc(sketch, "E11.23.9", {"start": v(5.93, 26.73) * mm, "mid": v(5.82, 26.86) * mm, "end": v(5.67, 26.93) * mm});
            skLineSegment(sketch, "E11.23.10", {"start": v(5.67, 26.93) * mm, "end": v(5.37, 27) * mm});
            skArc(sketch, "E11.23.11", {"start": v(6.23, 22.8) * mm, "mid": v(6.28, 22.53) * mm, "end": v(6.5, 22.36) * mm});
            skArc(sketch, "E11.23.12", {"start": v(2.55, 23.14) * mm, "mid": v(2.82, 23.21) * mm, "end": v(2.97, 23.45) * mm});
            skArc(sketch, "E12.trimOffspring", {"start": v(2.9, 23.1) * mm, "mid": v(1.7, 23.22) * mm, "end": v(0.49, 23.28) * mm});
            skArc(sketch, "E13.trimOffspring", {"start": v(8.78, 21.56) * mm, "mid": v(7.65, 22) * mm, "end": v(6.5, 22.36) * mm});
            skArc(sketch, "E14.trimOffspring", {"start": v(14.06, 18.56) * mm, "mid": v(13.08, 19.26) * mm, "end": v(12.06, 19.92) * mm});
            skArc(sketch, "E15.trimOffspring", {"start": v(-9.04, 21.46) * mm, "mid": v(-10.14, 20.96) * mm, "end": v(-11.22, 20.4) * mm});
            skArc(sketch, "E16.trimOffspring", {"start": v(18.39, 14.28) * mm, "mid": v(17.62, 15.22) * mm, "end": v(16.8, 16.12) * mm});
            skArc(sketch, "E17.trimOffspring", {"start": v(21.46, 9.04) * mm, "mid": v(20.96, 10.14) * mm, "end": v(20.4, 11.22) * mm});
            skArc(sketch, "E18.trimOffspring", {"start": v(-14.28, 18.39) * mm, "mid": v(-15.22, 17.62) * mm, "end": v(-16.12, 16.8) * mm});
            skArc(sketch, "E19.trimOffspring", {"start": v(-18.56, 14.06) * mm, "mid": v(-19.26, 13.08) * mm, "end": v(-19.92, 12.06) * mm});
            skArc(sketch, "E20.trimOffspring", {"start": v(-21.56, 8.78) * mm, "mid": v(-22, 7.65) * mm, "end": v(-22.36, 6.5) * mm});
            skArc(sketch, "E21.trimOffspring", {"start": v(-23.1, 2.9) * mm, "mid": v(-23.22, 1.7) * mm, "end": v(-23.28, 0.49) * mm});
            skArc(sketch, "E22.trimOffspring", {"start": v(-23.07, -3.18) * mm, "mid": v(-22.87, -4.37) * mm, "end": v(-22.61, -5.55) * mm});
            skArc(sketch, "E23.trimOffspring", {"start": v(-21.46, -9.04) * mm, "mid": v(-20.96, -10.14) * mm, "end": v(-20.4, -11.22) * mm});
            skArc(sketch, "E24.trimOffspring", {"start": v(-18.39, -14.28) * mm, "mid": v(-17.62, -15.22) * mm, "end": v(-16.8, -16.12) * mm});
            skArc(sketch, "E25.trimOffspring", {"start": v(23.07, 3.18) * mm, "mid": v(22.87, 4.37) * mm, "end": v(22.61, 5.55) * mm});
            skArc(sketch, "E26.trimOffspring", {"start": v(23.1, -2.9) * mm, "mid": v(23.22, -1.7) * mm, "end": v(23.28, -0.49) * mm});
            skArc(sketch, "E27.trimOffspring", {"start": v(21.56, -8.78) * mm, "mid": v(22, -7.65) * mm, "end": v(22.36, -6.5) * mm});
            skArc(sketch, "E28.trimOffspring", {"start": v(18.56, -14.06) * mm, "mid": v(19.26, -13.08) * mm, "end": v(19.92, -12.06) * mm});
            skArc(sketch, "E29.trimOffspring", {"start": v(-14.06, -18.56) * mm, "mid": v(-10.45, -20.8) * mm, "end": v(-6.5, -22.36) * mm});
            skArc(sketch, "E30.trimOffspring", {"start": v(14.28, -18.39) * mm, "mid": v(15.22, -17.62) * mm, "end": v(16.12, -16.8) * mm});
            skArc(sketch, "E31.trimOffspring", {"start": v(9.04, -21.46) * mm, "mid": v(10.14, -20.96) * mm, "end": v(11.22, -20.4) * mm});
            skArc(sketch, "E32.trimOffspring", {"start": v(3.18, -23.07) * mm, "mid": v(4.37, -22.87) * mm, "end": v(5.55, -22.61) * mm});
            skArc(sketch, "E33.trimOffspring", {"start": v(-2.9, -23.1) * mm, "mid": v(-1.7, -23.22) * mm, "end": v(-0.49, -23.28) * mm});
            skSolve(sketch);
        }
        {
            var Q0;
            Q0 = qSketchRegion(id + "F0", true);
            extrude(context, id + "F1", {"entities" : qUnion([Q0]), "depth" : 12.7 * mm});
        }
        {
            var Q0;
            Q0=makeQuery(id+"F1.opExtrude","CAP_FACE",FACE,{"disambiguationData":[OSD([sQuery(id+"F0.wireOp",EDGE,"E0"),sQuery(id+"F0.wireOp",EDGE,"E1.trimOffspring"),sQuery(id+"F0.wireOp",EDGE,"E2"),sQuery(id+"F0.wireOp",EDGE,"E3"),sQuery(id+"F0.wireOp",EDGE,"E4.MirrorCS"),sQuery(id+"F0.wireOp",EDGE,"E5.MirrorCS"),sQuery(id+"F0.wireOp",EDGE,"E6.MirrorCS"),sQuery(id+"F0.wireOp",EDGE,"E7.filletArc"),sQuery(id+"F0.wireOp",EDGE,"E8.filletArc"),sQuery(id+"F0.wireOp",EDGE,"E9.filletArc"),sQuery(id+"F0.wireOp",EDGE,"E10.filletArc"),sQuery(id+"F0.wireOp",EDGE,"E11.1.2"),sQuery(id+"F0.wireOp",EDGE,"E11.1.3"),sQuery(id+"F0.wireOp",EDGE,"E11.1.4"),sQuery(id+"F0.wireOp",EDGE,"E11.1.6"),sQuery(id+"F0.wireOp",EDGE,"E11.1.7"),sQuery(id+"F0.wireOp",EDGE,"E11.1.8"),sQuery(id+"F0.wireOp",EDGE,"E11.1.9"),sQuery(id+"F0.wireOp",EDGE,"E11.1.10"),sQuery(id+"F0.wireOp",EDGE,"E11.1.11"),sQuery(id+"F0.wireOp",EDGE,"E11.1.12"),sQuery(id+"F0.wireOp",EDGE,"E11.2.2"),sQuery(id+"F0.wireOp",EDGE,"E11.2.3"),sQuery(id+"F0.wireOp",EDGE,"E11.2.4"),sQuery(id+"F0.wireOp",EDGE,"E11.2.6"),sQuery(id+"F0.wireOp",EDGE,"E11.2.7"),sQuery(id+"F0.wireOp",EDGE,"E11.2.8"),sQuery(id+"F0.wireOp",EDGE,"E11.2.9"),sQuery(id+"F0.wireOp",EDGE,"E11.2.10"),sQuery(id+"F0.wireOp",EDGE,"E11.2.11"),sQuery(id+"F0.wireOp",EDGE,"E11.2.12"),sQuery(id+"F0.wireOp",EDGE,"E11.3.2"),sQuery(id+"F0.wireOp",EDGE,"E11.3.3"),sQuery(id+"F0.wireOp",EDGE,"E11.3.4"),sQuery(id+"F0.wireOp",EDGE,"E11.3.6"),sQuery(id+"F0.wireOp",EDGE,"E11.3.7"),sQuery(id+"F0.wireOp",EDGE,"E11.3.8"),sQuery(id+"F0.wireOp",EDGE,"E11.3.9"),sQuery(id+"F0.wireOp",EDGE,"E11.3.10"),sQuery(id+"F0.wireOp",EDGE,"E11.3.11"),sQuery(id+"F0.wireOp",EDGE,"E11.3.12"),sQuery(id+"F0.wireOp",EDGE,"E11.4.2"),sQuery(id+"F0.wireOp",EDGE,"E11.4.3"),sQuery(id+"F0.wireOp",EDGE,"E11.4.4"),sQuery(id+"F0.wireOp",EDGE,"E11.4.6"),sQuery(id+"F0.wireOp",EDGE,"E11.4.7"),sQuery(id+"F0.wireOp",EDGE,"E11.4.8"),sQuery(id+"F0.wireOp",EDGE,"E11.4.9"),sQuery(id+"F0.wireOp",EDGE,"E11.4.10"),sQuery(id+"F0.wireOp",EDGE,"E11.4.11"),sQuery(id+"F0.wireOp",EDGE,"E11.4.12"),sQuery(id+"F0.wireOp",EDGE,"E11.5.2"),sQuery(id+"F0.wireOp",EDGE,"E11.5.3"),sQuery(id+"F0.wireOp",EDGE,"E11.5.4"),sQuery(id+"F0.wireOp",EDGE,"E11.5.6"),sQuery(id+"F0.wireOp",EDGE,"E11.5.7"),sQuery(id+"F0.wireOp",EDGE,"E11.5.8"),sQuery(id+"F0.wireOp",EDGE,"E11.5.9"),sQuery(id+"F0.wireOp",EDGE,"E11.5.10"),sQuery(id+"F0.wireOp",EDGE,"E11.5.11"),sQuery(id+"F0.wireOp",EDGE,"E11.5.12"),sQuery(id+"F0.wireOp",EDGE,"E11.6.2"),sQuery(id+"F0.wireOp",EDGE,"E11.6.3"),sQuery(id+"F0.wireOp",EDGE,"E11.6.4"),sQuery(id+"F0.wireOp",EDGE,"E11.6.6"),sQuery(id+"F0.wireOp",EDGE,"E11.6.7"),sQuery(id+"F0.wireOp",EDGE,"E11.6.8"),sQuery(id+"F0.wireOp",EDGE,"E11.6.9"),sQuery(id+"F0.wireOp",EDGE,"E11.6.10"),sQuery(id+"F0.wireOp",EDGE,"E11.6.11"),sQuery(id+"F0.wireOp",EDGE,"E11.6.12"),sQuery(id+"F0.wireOp",EDGE,"E11.7.2"),sQuery(id+"F0.wireOp",EDGE,"E11.7.3"),sQuery(id+"F0.wireOp",EDGE,"E11.7.4"),sQuery(id+"F0.wireOp",EDGE,"E11.7.6"),sQuery(id+"F0.wireOp",EDGE,"E11.7.7"),sQuery(id+"F0.wireOp",EDGE,"E11.7.8"),sQuery(id+"F0.wireOp",EDGE,"E11.7.9"),sQuery(id+"F0.wireOp",EDGE,"E11.7.10"),sQuery(id+"F0.wireOp",EDGE,"E11.7.11"),sQuery(id+"F0.wireOp",EDGE,"E11.7.12"),sQuery(id+"F0.wireOp",EDGE,"E11.8.2"),sQuery(id+"F0.wireOp",EDGE,"E11.8.3"),sQuery(id+"F0.wireOp",EDGE,"E11.8.4"),sQuery(id+"F0.wireOp",EDGE,"E11.8.6"),sQuery(id+"F0.wireOp",EDGE,"E11.8.7"),sQuery(id+"F0.wireOp",EDGE,"E11.8.8"),sQuery(id+"F0.wireOp",EDGE,"E11.8.9"),sQuery(id+"F0.wireOp",EDGE,"E11.8.10"),sQuery(id+"F0.wireOp",EDGE,"E11.8.11"),sQuery(id+"F0.wireOp",EDGE,"E11.8.12"),sQuery(id+"F0.wireOp",EDGE,"E11.9.2"),sQuery(id+"F0.wireOp",EDGE,"E11.9.3"),sQuery(id+"F0.wireOp",EDGE,"E11.9.4"),sQuery(id+"F0.wireOp",EDGE,"E11.9.6"),sQuery(id+"F0.wireOp",EDGE,"E11.9.7"),sQuery(id+"F0.wireOp",EDGE,"E11.9.8"),sQuery(id+"F0.wireOp",EDGE,"E11.9.9"),sQuery(id+"F0.wireOp",EDGE,"E11.9.10"),sQuery(id+"F0.wireOp",EDGE,"E11.9.11"),sQuery(id+"F0.wireOp",EDGE,"E11.9.12"),sQuery(id+"F0.wireOp",EDGE,"E11.10.2"),sQuery(id+"F0.wireOp",EDGE,"E11.10.3"),sQuery(id+"F0.wireOp",EDGE,"E11.10.4"),sQuery(id+"F0.wireOp",EDGE,"E11.10.6"),sQuery(id+"F0.wireOp",EDGE,"E11.10.7"),sQuery(id+"F0.wireOp",EDGE,"E11.10.8"),sQuery(id+"F0.wireOp",EDGE,"E11.10.9"),sQuery(id+"F0.wireOp",EDGE,"E11.10.10"),sQuery(id+"F0.wireOp",EDGE,"E11.10.11"),sQuery(id+"F0.wireOp",EDGE,"E11.10.12"),sQuery(id+"F0.wireOp",EDGE,"E11.11.2"),sQuery(id+"F0.wireOp",EDGE,"E11.11.3"),sQuery(id+"F0.wireOp",EDGE,"E11.11.4"),sQuery(id+"F0.wireOp",EDGE,"E11.11.6"),sQuery(id+"F0.wireOp",EDGE,"E11.11.7"),sQuery(id+"F0.wireOp",EDGE,"E11.11.8"),sQuery(id+"F0.wireOp",EDGE,"E11.11.9"),sQuery(id+"F0.wireOp",EDGE,"E11.11.10"),sQuery(id+"F0.wireOp",EDGE,"E11.11.11"),sQuery(id+"F0.wireOp",EDGE,"E11.11.12"),sQuery(id+"F0.wireOp",EDGE,"E11.12.2"),sQuery(id+"F0.wireOp",EDGE,"E11.12.3"),sQuery(id+"F0.wireOp",EDGE,"E11.12.4"),sQuery(id+"F0.wireOp",EDGE,"E11.12.6"),sQuery(id+"F0.wireOp",EDGE,"E11.12.7"),sQuery(id+"F0.wireOp",EDGE,"E11.12.8"),sQuery(id+"F0.wireOp",EDGE,"E11.12.9"),sQuery(id+"F0.wireOp",EDGE,"E11.12.10"),sQuery(id+"F0.wireOp",EDGE,"E11.12.11"),sQuery(id+"F0.wireOp",EDGE,"E11.12.12"),sQuery(id+"F0.wireOp",EDGE,"E11.13.2"),sQuery(id+"F0.wireOp",EDGE,"E11.13.3"),sQuery(id+"F0.wireOp",EDGE,"E11.13.4"),sQuery(id+"F0.wireOp",EDGE,"E11.13.6"),sQuery(id+"F0.wireOp",EDGE,"E11.13.7"),sQuery(id+"F0.wireOp",EDGE,"E11.13.8"),sQuery(id+"F0.wireOp",EDGE,"E11.13.9"),sQuery(id+"F0.wireOp",EDGE,"E11.13.10"),sQuery(id+"F0.wireOp",EDGE,"E11.13.11"),sQuery(id+"F0.wireOp",EDGE,"E11.13.12"),sQuery(id+"F0.wireOp",EDGE,"E11.14.2"),sQuery(id+"F0.wireOp",EDGE,"E11.14.3"),sQuery(id+"F0.wireOp",EDGE,"E11.14.4"),sQuery(id+"F0.wireOp",EDGE,"E11.14.6"),sQuery(id+"F0.wireOp",EDGE,"E11.14.7"),sQuery(id+"F0.wireOp",EDGE,"E11.14.8"),sQuery(id+"F0.wireOp",EDGE,"E11.14.9"),sQuery(id+"F0.wireOp",EDGE,"E11.14.10"),sQuery(id+"F0.wireOp",EDGE,"E11.14.11"),sQuery(id+"F0.wireOp",EDGE,"E11.14.12"),sQuery(id+"F0.wireOp",EDGE,"E11.15.2"),sQuery(id+"F0.wireOp",EDGE,"E11.15.3"),sQuery(id+"F0.wireOp",EDGE,"E11.15.4"),sQuery(id+"F0.wireOp",EDGE,"E11.15.6"),sQuery(id+"F0.wireOp",EDGE,"E11.15.7"),sQuery(id+"F0.wireOp",EDGE,"E11.15.8"),sQuery(id+"F0.wireOp",EDGE,"E11.15.9"),sQuery(id+"F0.wireOp",EDGE,"E11.15.10"),sQuery(id+"F0.wireOp",EDGE,"E11.15.11"),sQuery(id+"F0.wireOp",EDGE,"E11.15.12"),sQuery(id+"F0.wireOp",EDGE,"E11.16.2"),sQuery(id+"F0.wireOp",EDGE,"E11.16.3"),sQuery(id+"F0.wireOp",EDGE,"E11.16.4"),sQuery(id+"F0.wireOp",EDGE,"E11.16.6"),sQuery(id+"F0.wireOp",EDGE,"E11.16.7"),sQuery(id+"F0.wireOp",EDGE,"E11.16.8"),sQuery(id+"F0.wireOp",EDGE,"E11.16.9"),sQuery(id+"F0.wireOp",EDGE,"E11.16.10"),sQuery(id+"F0.wireOp",EDGE,"E11.16.11"),sQuery(id+"F0.wireOp",EDGE,"E11.16.12"),sQuery(id+"F0.wireOp",EDGE,"E11.17.2"),sQuery(id+"F0.wireOp",EDGE,"E11.17.3"),sQuery(id+"F0.wireOp",EDGE,"E11.17.4"),sQuery(id+"F0.wireOp",EDGE,"E11.17.6"),sQuery(id+"F0.wireOp",EDGE,"E11.17.7"),sQuery(id+"F0.wireOp",EDGE,"E11.17.8"),sQuery(id+"F0.wireOp",EDGE,"E11.17.9"),sQuery(id+"F0.wireOp",EDGE,"E11.17.10"),sQuery(id+"F0.wireOp",EDGE,"E11.17.11"),sQuery(id+"F0.wireOp",EDGE,"E11.17.12"),sQuery(id+"F0.wireOp",EDGE,"E11.18.2"),sQuery(id+"F0.wireOp",EDGE,"E11.18.3"),sQuery(id+"F0.wireOp",EDGE,"E11.18.4"),sQuery(id+"F0.wireOp",EDGE,"E11.18.6"),sQuery(id+"F0.wireOp",EDGE,"E11.18.7"),sQuery(id+"F0.wireOp",EDGE,"E11.18.8"),sQuery(id+"F0.wireOp",EDGE,"E11.18.9"),sQuery(id+"F0.wireOp",EDGE,"E11.18.10"),sQuery(id+"F0.wireOp",EDGE,"E11.18.11"),sQuery(id+"F0.wireOp",EDGE,"E11.18.12"),sQuery(id+"F0.wireOp",EDGE,"E11.19.2"),sQuery(id+"F0.wireOp",EDGE,"E11.19.3"),sQuery(id+"F0.wireOp",EDGE,"E11.19.4"),sQuery(id+"F0.wireOp",EDGE,"E11.19.6"),sQuery(id+"F0.wireOp",EDGE,"E11.19.7"),sQuery(id+"F0.wireOp",EDGE,"E11.19.8"),sQuery(id+"F0.wireOp",EDGE,"E11.19.9"),sQuery(id+"F0.wireOp",EDGE,"E11.19.10"),sQuery(id+"F0.wireOp",EDGE,"E11.19.11"),sQuery(id+"F0.wireOp",EDGE,"E11.19.12"),sQuery(id+"F0.wireOp",EDGE,"E11.20.2"),sQuery(id+"F0.wireOp",EDGE,"E11.20.3"),sQuery(id+"F0.wireOp",EDGE,"E11.20.4"),sQuery(id+"F0.wireOp",EDGE,"E11.20.6"),sQuery(id+"F0.wireOp",EDGE,"E11.20.7"),sQuery(id+"F0.wireOp",EDGE,"E11.20.8"),sQuery(id+"F0.wireOp",EDGE,"E11.20.9"),sQuery(id+"F0.wireOp",EDGE,"E11.20.10"),sQuery(id+"F0.wireOp",EDGE,"E11.20.11"),sQuery(id+"F0.wireOp",EDGE,"E11.20.12"),sQuery(id+"F0.wireOp",EDGE,"E11.21.2"),sQuery(id+"F0.wireOp",EDGE,"E11.21.3"),sQuery(id+"F0.wireOp",EDGE,"E11.21.4"),sQuery(id+"F0.wireOp",EDGE,"E11.21.6"),sQuery(id+"F0.wireOp",EDGE,"E11.21.7"),sQuery(id+"F0.wireOp",EDGE,"E11.21.8"),sQuery(id+"F0.wireOp",EDGE,"E11.21.9"),sQuery(id+"F0.wireOp",EDGE,"E11.21.10"),sQuery(id+"F0.wireOp",EDGE,"E11.21.11"),sQuery(id+"F0.wireOp",EDGE,"E11.21.12"),sQuery(id+"F0.wireOp",EDGE,"E11.22.2"),sQuery(id+"F0.wireOp",EDGE,"E11.22.3"),sQuery(id+"F0.wireOp",EDGE,"E11.22.4"),sQuery(id+"F0.wireOp",EDGE,"E11.22.6"),sQuery(id+"F0.wireOp",EDGE,"E11.22.7"),sQuery(id+"F0.wireOp",EDGE,"E11.22.8"),sQuery(id+"F0.wireOp",EDGE,"E11.22.9"),sQuery(id+"F0.wireOp",EDGE,"E11.22.10"),sQuery(id+"F0.wireOp",EDGE,"E11.22.11"),sQuery(id+"F0.wireOp",EDGE,"E11.22.12"),sQuery(id+"F0.wireOp",EDGE,"E11.23.2"),sQuery(id+"F0.wireOp",EDGE,"E11.23.3"),sQuery(id+"F0.wireOp",EDGE,"E11.23.4"),sQuery(id+"F0.wireOp",EDGE,"E11.23.6"),sQuery(id+"F0.wireOp",EDGE,"E11.23.7"),sQuery(id+"F0.wireOp",EDGE,"E11.23.8"),sQuery(id+"F0.wireOp",EDGE,"E11.23.9"),sQuery(id+"F0.wireOp",EDGE,"E11.23.10"),sQuery(id+"F0.wireOp",EDGE,"E11.23.11"),sQuery(id+"F0.wireOp",EDGE,"E11.23.12"),sQuery(id+"F0.wireOp",EDGE,"E12.trimOffspring"),sQuery(id+"F0.wireOp",EDGE,"E13.trimOffspring"),sQuery(id+"F0.wireOp",EDGE,"E14.trimOffspring"),sQuery(id+"F0.wireOp",EDGE,"E15.trimOffspring"),sQuery(id+"F0.wireOp",EDGE,"E16.trimOffspring"),sQuery(id+"F0.wireOp",EDGE,"E17.trimOffspring"),sQuery(id+"F0.wireOp",EDGE,"E18.trimOffspring"),sQuery(id+"F0.wireOp",EDGE,"E19.trimOffspring"),sQuery(id+"F0.wireOp",EDGE,"E20.trimOffspring"),sQuery(id+"F0.wireOp",EDGE,"E21.trimOffspring"),sQuery(id+"F0.wireOp",EDGE,"E22.trimOffspring"),sQuery(id+"F0.wireOp",EDGE,"E23.trimOffspring"),sQuery(id+"F0.wireOp",EDGE,"E24.trimOffspring"),sQuery(id+"F0.wireOp",EDGE,"E25.trimOffspring"),sQuery(id+"F0.wireOp",EDGE,"E26.trimOffspring"),sQuery(id+"F0.wireOp",EDGE,"E27.trimOffspring"),sQuery(id+"F0.wireOp",EDGE,"E28.trimOffspring"),sQuery(id+"F0.wireOp",EDGE,"E29.trimOffspring"),sQuery(id+"F0.wireOp",EDGE,"E30.trimOffspring"),sQuery(id+"F0.wireOp",EDGE,"E31.trimOffspring"),sQuery(id+"F0.wireOp",EDGE,"E32.trimOffspring"),sQuery(id+"F0.wireOp",EDGE,"E33.trimOffspring")])],"isStart":false});
            var sketch = newSketch(context, id + "F2", { "sketchPlane" : qUnion([Q0])});
            skPoint(sketch, "E34", {"position": v(0, 0) * mm});
            skSolve(sketch);
        }
        {
            var Q0;
            Q0=sQuery(id+"F2.wireOp",VERTEX,"E34");
            var Q1;
            Q1=makeQuery(id+"F1.opExtrude","SWEPT_BODY",BODY,{"disambiguationData":[OSD([sQuery(id+"F0.wireOp",EDGE,"E0"),sQuery(id+"F0.wireOp",EDGE,"E1.trimOffspring"),sQuery(id+"F0.wireOp",EDGE,"E2"),sQuery(id+"F0.wireOp",EDGE,"E3"),sQuery(id+"F0.wireOp",EDGE,"E4.MirrorCS"),sQuery(id+"F0.wireOp",EDGE,"E5.MirrorCS"),sQuery(id+"F0.wireOp",EDGE,"E6.MirrorCS"),sQuery(id+"F0.wireOp",EDGE,"E7.filletArc"),sQuery(id+"F0.wireOp",EDGE,"E8.filletArc"),sQuery(id+"F0.wireOp",EDGE,"E9.filletArc"),sQuery(id+"F0.wireOp",EDGE,"E10.filletArc"),sQuery(id+"F0.wireOp",EDGE,"E11.1.2"),sQuery(id+"F0.wireOp",EDGE,"E11.1.3"),sQuery(id+"F0.wireOp",EDGE,"E11.1.4"),sQuery(id+"F0.wireOp",EDGE,"E11.1.6"),sQuery(id+"F0.wireOp",EDGE,"E11.1.7"),sQuery(id+"F0.wireOp",EDGE,"E11.1.8"),sQuery(id+"F0.wireOp",EDGE,"E11.1.9"),sQuery(id+"F0.wireOp",EDGE,"E11.1.10"),sQuery(id+"F0.wireOp",EDGE,"E11.1.11"),sQuery(id+"F0.wireOp",EDGE,"E11.1.12"),sQuery(id+"F0.wireOp",EDGE,"E11.2.2"),sQuery(id+"F0.wireOp",EDGE,"E11.2.3"),sQuery(id+"F0.wireOp",EDGE,"E11.2.4"),sQuery(id+"F0.wireOp",EDGE,"E11.2.6"),sQuery(id+"F0.wireOp",EDGE,"E11.2.7"),sQuery(id+"F0.wireOp",EDGE,"E11.2.8"),sQuery(id+"F0.wireOp",EDGE,"E11.2.9"),sQuery(id+"F0.wireOp",EDGE,"E11.2.10"),sQuery(id+"F0.wireOp",EDGE,"E11.2.11"),sQuery(id+"F0.wireOp",EDGE,"E11.2.12"),sQuery(id+"F0.wireOp",EDGE,"E11.3.2"),sQuery(id+"F0.wireOp",EDGE,"E11.3.3"),sQuery(id+"F0.wireOp",EDGE,"E11.3.4"),sQuery(id+"F0.wireOp",EDGE,"E11.3.6"),sQuery(id+"F0.wireOp",EDGE,"E11.3.7"),sQuery(id+"F0.wireOp",EDGE,"E11.3.8"),sQuery(id+"F0.wireOp",EDGE,"E11.3.9"),sQuery(id+"F0.wireOp",EDGE,"E11.3.10"),sQuery(id+"F0.wireOp",EDGE,"E11.3.11"),sQuery(id+"F0.wireOp",EDGE,"E11.3.12"),sQuery(id+"F0.wireOp",EDGE,"E11.4.2"),sQuery(id+"F0.wireOp",EDGE,"E11.4.3"),sQuery(id+"F0.wireOp",EDGE,"E11.4.4"),sQuery(id+"F0.wireOp",EDGE,"E11.4.6"),sQuery(id+"F0.wireOp",EDGE,"E11.4.7"),sQuery(id+"F0.wireOp",EDGE,"E11.4.8"),sQuery(id+"F0.wireOp",EDGE,"E11.4.9"),sQuery(id+"F0.wireOp",EDGE,"E11.4.10"),sQuery(id+"F0.wireOp",EDGE,"E11.4.11"),sQuery(id+"F0.wireOp",EDGE,"E11.4.12"),sQuery(id+"F0.wireOp",EDGE,"E11.5.2"),sQuery(id+"F0.wireOp",EDGE,"E11.5.3"),sQuery(id+"F0.wireOp",EDGE,"E11.5.4"),sQuery(id+"F0.wireOp",EDGE,"E11.5.6"),sQuery(id+"F0.wireOp",EDGE,"E11.5.7"),sQuery(id+"F0.wireOp",EDGE,"E11.5.8"),sQuery(id+"F0.wireOp",EDGE,"E11.5.9"),sQuery(id+"F0.wireOp",EDGE,"E11.5.10"),sQuery(id+"F0.wireOp",EDGE,"E11.5.11"),sQuery(id+"F0.wireOp",EDGE,"E11.5.12"),sQuery(id+"F0.wireOp",EDGE,"E11.6.2"),sQuery(id+"F0.wireOp",EDGE,"E11.6.3"),sQuery(id+"F0.wireOp",EDGE,"E11.6.4"),sQuery(id+"F0.wireOp",EDGE,"E11.6.6"),sQuery(id+"F0.wireOp",EDGE,"E11.6.7"),sQuery(id+"F0.wireOp",EDGE,"E11.6.8"),sQuery(id+"F0.wireOp",EDGE,"E11.6.9"),sQuery(id+"F0.wireOp",EDGE,"E11.6.10"),sQuery(id+"F0.wireOp",EDGE,"E11.6.11"),sQuery(id+"F0.wireOp",EDGE,"E11.6.12"),sQuery(id+"F0.wireOp",EDGE,"E11.7.2"),sQuery(id+"F0.wireOp",EDGE,"E11.7.3"),sQuery(id+"F0.wireOp",EDGE,"E11.7.4"),sQuery(id+"F0.wireOp",EDGE,"E11.7.6"),sQuery(id+"F0.wireOp",EDGE,"E11.7.7"),sQuery(id+"F0.wireOp",EDGE,"E11.7.8"),sQuery(id+"F0.wireOp",EDGE,"E11.7.9"),sQuery(id+"F0.wireOp",EDGE,"E11.7.10"),sQuery(id+"F0.wireOp",EDGE,"E11.7.11"),sQuery(id+"F0.wireOp",EDGE,"E11.7.12"),sQuery(id+"F0.wireOp",EDGE,"E11.8.2"),sQuery(id+"F0.wireOp",EDGE,"E11.8.3"),sQuery(id+"F0.wireOp",EDGE,"E11.8.4"),sQuery(id+"F0.wireOp",EDGE,"E11.8.6"),sQuery(id+"F0.wireOp",EDGE,"E11.8.7"),sQuery(id+"F0.wireOp",EDGE,"E11.8.8"),sQuery(id+"F0.wireOp",EDGE,"E11.8.9"),sQuery(id+"F0.wireOp",EDGE,"E11.8.10"),sQuery(id+"F0.wireOp",EDGE,"E11.8.11"),sQuery(id+"F0.wireOp",EDGE,"E11.8.12"),sQuery(id+"F0.wireOp",EDGE,"E11.9.2"),sQuery(id+"F0.wireOp",EDGE,"E11.9.3"),sQuery(id+"F0.wireOp",EDGE,"E11.9.4"),sQuery(id+"F0.wireOp",EDGE,"E11.9.6"),sQuery(id+"F0.wireOp",EDGE,"E11.9.7"),sQuery(id+"F0.wireOp",EDGE,"E11.9.8"),sQuery(id+"F0.wireOp",EDGE,"E11.9.9"),sQuery(id+"F0.wireOp",EDGE,"E11.9.10"),sQuery(id+"F0.wireOp",EDGE,"E11.9.11"),sQuery(id+"F0.wireOp",EDGE,"E11.9.12"),sQuery(id+"F0.wireOp",EDGE,"E11.10.2"),sQuery(id+"F0.wireOp",EDGE,"E11.10.3"),sQuery(id+"F0.wireOp",EDGE,"E11.10.4"),sQuery(id+"F0.wireOp",EDGE,"E11.10.6"),sQuery(id+"F0.wireOp",EDGE,"E11.10.7"),sQuery(id+"F0.wireOp",EDGE,"E11.10.8"),sQuery(id+"F0.wireOp",EDGE,"E11.10.9"),sQuery(id+"F0.wireOp",EDGE,"E11.10.10"),sQuery(id+"F0.wireOp",EDGE,"E11.10.11"),sQuery(id+"F0.wireOp",EDGE,"E11.10.12"),sQuery(id+"F0.wireOp",EDGE,"E11.11.2"),sQuery(id+"F0.wireOp",EDGE,"E11.11.3"),sQuery(id+"F0.wireOp",EDGE,"E11.11.4"),sQuery(id+"F0.wireOp",EDGE,"E11.11.6"),sQuery(id+"F0.wireOp",EDGE,"E11.11.7"),sQuery(id+"F0.wireOp",EDGE,"E11.11.8"),sQuery(id+"F0.wireOp",EDGE,"E11.11.9"),sQuery(id+"F0.wireOp",EDGE,"E11.11.10"),sQuery(id+"F0.wireOp",EDGE,"E11.11.11"),sQuery(id+"F0.wireOp",EDGE,"E11.11.12"),sQuery(id+"F0.wireOp",EDGE,"E11.12.2"),sQuery(id+"F0.wireOp",EDGE,"E11.12.3"),sQuery(id+"F0.wireOp",EDGE,"E11.12.4"),sQuery(id+"F0.wireOp",EDGE,"E11.12.6"),sQuery(id+"F0.wireOp",EDGE,"E11.12.7"),sQuery(id+"F0.wireOp",EDGE,"E11.12.8"),sQuery(id+"F0.wireOp",EDGE,"E11.12.9"),sQuery(id+"F0.wireOp",EDGE,"E11.12.10"),sQuery(id+"F0.wireOp",EDGE,"E11.12.11"),sQuery(id+"F0.wireOp",EDGE,"E11.12.12"),sQuery(id+"F0.wireOp",EDGE,"E11.13.2"),sQuery(id+"F0.wireOp",EDGE,"E11.13.3"),sQuery(id+"F0.wireOp",EDGE,"E11.13.4"),sQuery(id+"F0.wireOp",EDGE,"E11.13.6"),sQuery(id+"F0.wireOp",EDGE,"E11.13.7"),sQuery(id+"F0.wireOp",EDGE,"E11.13.8"),sQuery(id+"F0.wireOp",EDGE,"E11.13.9"),sQuery(id+"F0.wireOp",EDGE,"E11.13.10"),sQuery(id+"F0.wireOp",EDGE,"E11.13.11"),sQuery(id+"F0.wireOp",EDGE,"E11.13.12"),sQuery(id+"F0.wireOp",EDGE,"E11.14.2"),sQuery(id+"F0.wireOp",EDGE,"E11.14.3"),sQuery(id+"F0.wireOp",EDGE,"E11.14.4"),sQuery(id+"F0.wireOp",EDGE,"E11.14.6"),sQuery(id+"F0.wireOp",EDGE,"E11.14.7"),sQuery(id+"F0.wireOp",EDGE,"E11.14.8"),sQuery(id+"F0.wireOp",EDGE,"E11.14.9"),sQuery(id+"F0.wireOp",EDGE,"E11.14.10"),sQuery(id+"F0.wireOp",EDGE,"E11.14.11"),sQuery(id+"F0.wireOp",EDGE,"E11.14.12"),sQuery(id+"F0.wireOp",EDGE,"E11.15.2"),sQuery(id+"F0.wireOp",EDGE,"E11.15.3"),sQuery(id+"F0.wireOp",EDGE,"E11.15.4"),sQuery(id+"F0.wireOp",EDGE,"E11.15.6"),sQuery(id+"F0.wireOp",EDGE,"E11.15.7"),sQuery(id+"F0.wireOp",EDGE,"E11.15.8"),sQuery(id+"F0.wireOp",EDGE,"E11.15.9"),sQuery(id+"F0.wireOp",EDGE,"E11.15.10"),sQuery(id+"F0.wireOp",EDGE,"E11.15.11"),sQuery(id+"F0.wireOp",EDGE,"E11.15.12"),sQuery(id+"F0.wireOp",EDGE,"E11.16.2"),sQuery(id+"F0.wireOp",EDGE,"E11.16.3"),sQuery(id+"F0.wireOp",EDGE,"E11.16.4"),sQuery(id+"F0.wireOp",EDGE,"E11.16.6"),sQuery(id+"F0.wireOp",EDGE,"E11.16.7"),sQuery(id+"F0.wireOp",EDGE,"E11.16.8"),sQuery(id+"F0.wireOp",EDGE,"E11.16.9"),sQuery(id+"F0.wireOp",EDGE,"E11.16.10"),sQuery(id+"F0.wireOp",EDGE,"E11.16.11"),sQuery(id+"F0.wireOp",EDGE,"E11.16.12"),sQuery(id+"F0.wireOp",EDGE,"E11.17.2"),sQuery(id+"F0.wireOp",EDGE,"E11.17.3"),sQuery(id+"F0.wireOp",EDGE,"E11.17.4"),sQuery(id+"F0.wireOp",EDGE,"E11.17.6"),sQuery(id+"F0.wireOp",EDGE,"E11.17.7"),sQuery(id+"F0.wireOp",EDGE,"E11.17.8"),sQuery(id+"F0.wireOp",EDGE,"E11.17.9"),sQuery(id+"F0.wireOp",EDGE,"E11.17.10"),sQuery(id+"F0.wireOp",EDGE,"E11.17.11"),sQuery(id+"F0.wireOp",EDGE,"E11.17.12"),sQuery(id+"F0.wireOp",EDGE,"E11.18.2"),sQuery(id+"F0.wireOp",EDGE,"E11.18.3"),sQuery(id+"F0.wireOp",EDGE,"E11.18.4"),sQuery(id+"F0.wireOp",EDGE,"E11.18.6"),sQuery(id+"F0.wireOp",EDGE,"E11.18.7"),sQuery(id+"F0.wireOp",EDGE,"E11.18.8"),sQuery(id+"F0.wireOp",EDGE,"E11.18.9"),sQuery(id+"F0.wireOp",EDGE,"E11.18.10"),sQuery(id+"F0.wireOp",EDGE,"E11.18.11"),sQuery(id+"F0.wireOp",EDGE,"E11.18.12"),sQuery(id+"F0.wireOp",EDGE,"E11.19.2"),sQuery(id+"F0.wireOp",EDGE,"E11.19.3"),sQuery(id+"F0.wireOp",EDGE,"E11.19.4"),sQuery(id+"F0.wireOp",EDGE,"E11.19.6"),sQuery(id+"F0.wireOp",EDGE,"E11.19.7"),sQuery(id+"F0.wireOp",EDGE,"E11.19.8"),sQuery(id+"F0.wireOp",EDGE,"E11.19.9"),sQuery(id+"F0.wireOp",EDGE,"E11.19.10"),sQuery(id+"F0.wireOp",EDGE,"E11.19.11"),sQuery(id+"F0.wireOp",EDGE,"E11.19.12"),sQuery(id+"F0.wireOp",EDGE,"E11.20.2"),sQuery(id+"F0.wireOp",EDGE,"E11.20.3"),sQuery(id+"F0.wireOp",EDGE,"E11.20.4"),sQuery(id+"F0.wireOp",EDGE,"E11.20.6"),sQuery(id+"F0.wireOp",EDGE,"E11.20.7"),sQuery(id+"F0.wireOp",EDGE,"E11.20.8"),sQuery(id+"F0.wireOp",EDGE,"E11.20.9"),sQuery(id+"F0.wireOp",EDGE,"E11.20.10"),sQuery(id+"F0.wireOp",EDGE,"E11.20.11"),sQuery(id+"F0.wireOp",EDGE,"E11.20.12"),sQuery(id+"F0.wireOp",EDGE,"E11.21.2"),sQuery(id+"F0.wireOp",EDGE,"E11.21.3"),sQuery(id+"F0.wireOp",EDGE,"E11.21.4"),sQuery(id+"F0.wireOp",EDGE,"E11.21.6"),sQuery(id+"F0.wireOp",EDGE,"E11.21.7"),sQuery(id+"F0.wireOp",EDGE,"E11.21.8"),sQuery(id+"F0.wireOp",EDGE,"E11.21.9"),sQuery(id+"F0.wireOp",EDGE,"E11.21.10"),sQuery(id+"F0.wireOp",EDGE,"E11.21.11"),sQuery(id+"F0.wireOp",EDGE,"E11.21.12"),sQuery(id+"F0.wireOp",EDGE,"E11.22.2"),sQuery(id+"F0.wireOp",EDGE,"E11.22.3"),sQuery(id+"F0.wireOp",EDGE,"E11.22.4"),sQuery(id+"F0.wireOp",EDGE,"E11.22.6"),sQuery(id+"F0.wireOp",EDGE,"E11.22.7"),sQuery(id+"F0.wireOp",EDGE,"E11.22.8"),sQuery(id+"F0.wireOp",EDGE,"E11.22.9"),sQuery(id+"F0.wireOp",EDGE,"E11.22.10"),sQuery(id+"F0.wireOp",EDGE,"E11.22.11"),sQuery(id+"F0.wireOp",EDGE,"E11.22.12"),sQuery(id+"F0.wireOp",EDGE,"E11.23.2"),sQuery(id+"F0.wireOp",EDGE,"E11.23.3"),sQuery(id+"F0.wireOp",EDGE,"E11.23.4"),sQuery(id+"F0.wireOp",EDGE,"E11.23.6"),sQuery(id+"F0.wireOp",EDGE,"E11.23.7"),sQuery(id+"F0.wireOp",EDGE,"E11.23.8"),sQuery(id+"F0.wireOp",EDGE,"E11.23.9"),sQuery(id+"F0.wireOp",EDGE,"E11.23.10"),sQuery(id+"F0.wireOp",EDGE,"E11.23.11"),sQuery(id+"F0.wireOp",EDGE,"E11.23.12"),sQuery(id+"F0.wireOp",EDGE,"E12.trimOffspring"),sQuery(id+"F0.wireOp",EDGE,"E13.trimOffspring"),sQuery(id+"F0.wireOp",EDGE,"E14.trimOffspring"),sQuery(id+"F0.wireOp",EDGE,"E15.trimOffspring"),sQuery(id+"F0.wireOp",EDGE,"E16.trimOffspring"),sQuery(id+"F0.wireOp",EDGE,"E17.trimOffspring"),sQuery(id+"F0.wireOp",EDGE,"E18.trimOffspring"),sQuery(id+"F0.wireOp",EDGE,"E19.trimOffspring"),sQuery(id+"F0.wireOp",EDGE,"E20.trimOffspring"),sQuery(id+"F0.wireOp",EDGE,"E21.trimOffspring"),sQuery(id+"F0.wireOp",EDGE,"E22.trimOffspring"),sQuery(id+"F0.wireOp",EDGE,"E23.trimOffspring"),sQuery(id+"F0.wireOp",EDGE,"E24.trimOffspring"),sQuery(id+"F0.wireOp",EDGE,"E25.trimOffspring"),sQuery(id+"F0.wireOp",EDGE,"E26.trimOffspring"),sQuery(id+"F0.wireOp",EDGE,"E27.trimOffspring"),sQuery(id+"F0.wireOp",EDGE,"E28.trimOffspring"),sQuery(id+"F0.wireOp",EDGE,"E29.trimOffspring"),sQuery(id+"F0.wireOp",EDGE,"E30.trimOffspring"),sQuery(id+"F0.wireOp",EDGE,"E31.trimOffspring"),sQuery(id+"F0.wireOp",EDGE,"E32.trimOffspring"),sQuery(id+"F0.wireOp",EDGE,"E33.trimOffspring")])]});
            hole(context, id + "F3", {"style" : HoleStyle.SIMPLE, "endStyle" : HoleEndStyle.THROUGH, "holeDiameter" : 6.35 * mm, "locations" : qUnion([Q0]), "scope" : qUnion([Q1]), "isTappedThrough" : true});
        }
    });
